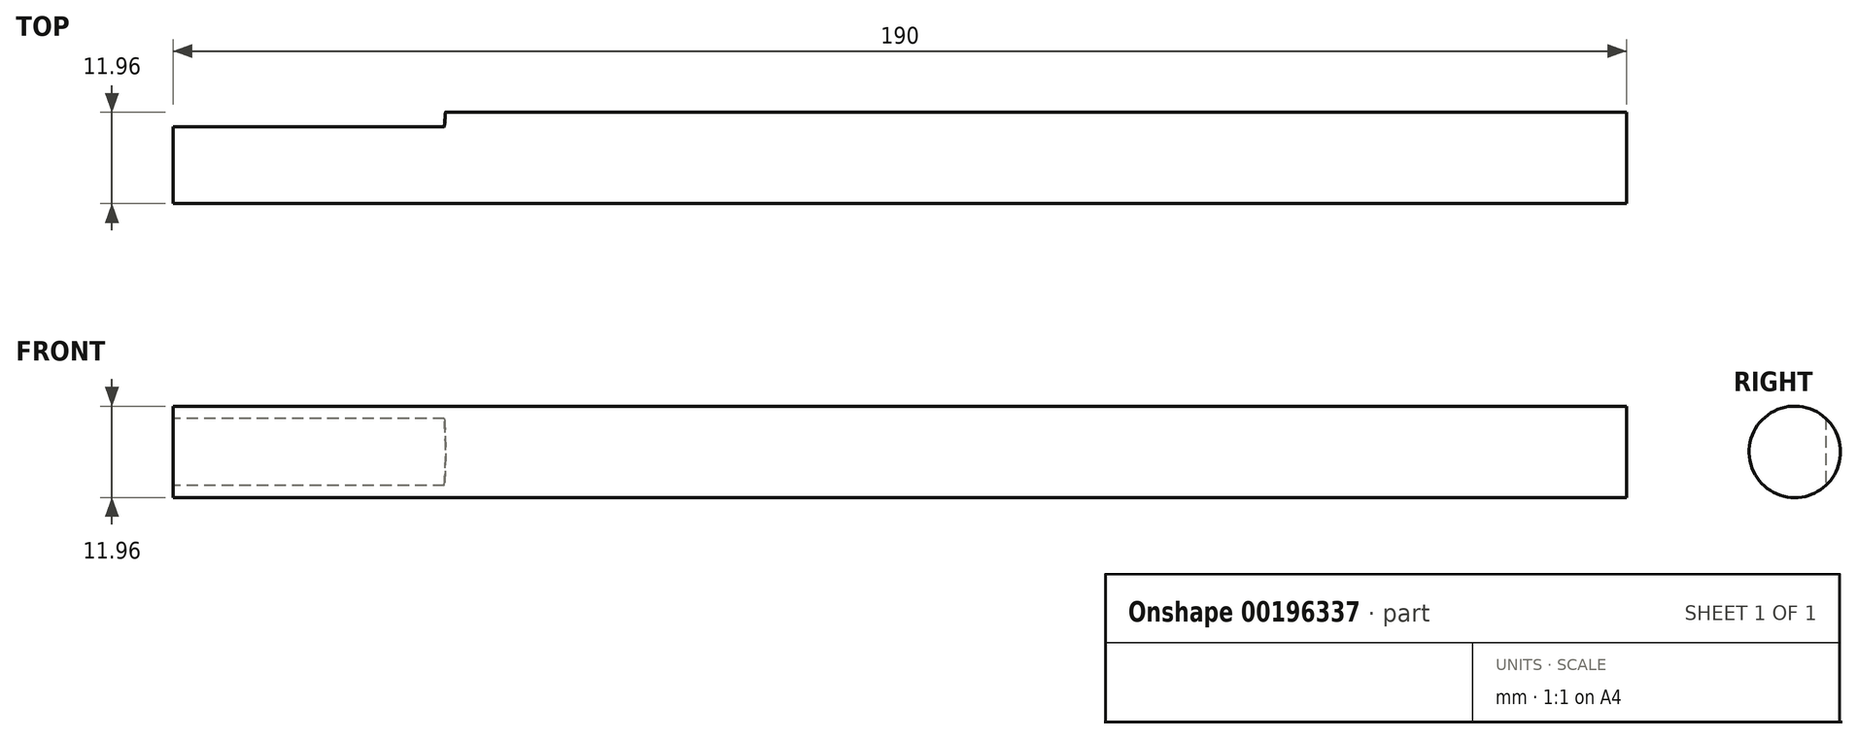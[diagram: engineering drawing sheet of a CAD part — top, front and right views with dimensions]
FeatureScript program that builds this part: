
annotation { "Feature Type Name" : "Feature", "Feature Type Description" : "" }
export const myFeature = defineFeature(function(context is Context, id is Id, definition is map)
    precondition{}
    {
        {
            var Q0;
            Q0=qCreatedBy(makeId("Right.planeOp"),FACE);
            var sketch = newSketch(context, id + "F0", { "sketchPlane" : qUnion([Q0])});
            skCircle(sketch, "E0", {"center": v(0, 0) * mm, "radius": 5.98 * mm});
            skSolve(sketch);
        }
        {
            var Q0;
            Q0 = qSketchRegion(id + "F0", true);
            extrude(context, id + "F1", {"entities" : qUnion([Q0]), "depth" : 200 * mm});
        }
        {
            var Q0;
            Q0=qCreatedBy(makeId("Top.planeOp"),FACE);
            var sketch = newSketch(context, id + "F2", { "sketchPlane" : qUnion([Q0])});
            skLineSegment(sketch, "E1", {"start": v(0, 6.11) * mm, "end": v(45.45, 6.11) * mm});
            skLineSegment(sketch, "E2", {"start": v(45.45, 6.11) * mm, "end": v(45.45, 4.07) * mm});
            skLineSegment(sketch, "E3", {"start": v(45.45, 4.07) * mm, "end": v(0, 4.07) * mm});
            skLineSegment(sketch, "E4", {"start": v(0, 4.07) * mm, "end": v(0, 6.11) * mm});
            skSolve(sketch);
        }
        {
            var Q0;
            Q0 = qSketchRegion(id + "F2", true);
            extrude(context, id + "F3", {"entities" : qUnion([Q0]), "operationType" : NewBodyOperationType.REMOVE, "endBound" : BoundingType.SYMMETRIC, "depth" : 25 * mm});
        }
        {
            var Q0;
            Q0=makeQuery(id+"F3.boolean.opBoolean","COPY",FACE,{"derivedFrom":makeQuery(id+"F3.opExtrude","SWEPT_FACE",FACE,{"disambiguationData":[OSD([sQuery(id+"F2.wireOp",EDGE,"E3")])]})});
            var sketch = newSketch(context, id + "F4", { "sketchPlane" : qUnion([Q0])});
            skLineSegment(sketch, "E5", {"start": v(-45.45, 0) * mm, "end": v(15.43, 0) * mm});
            skCircle(sketch, "E6", {"center": v(15.43, 0) * mm, "radius": 61.04 * mm});
            skSolve(sketch);
        }
        {
            var Q0;
            Q0 = qSketchRegion(id + "F4", true);
            extrude(context, id + "F5", {"entities" : qUnion([Q0]), "operationType" : NewBodyOperationType.REMOVE, "depth" : 25 * mm});
        }
        {
            var Q0;
            Q0=makeQuery(id+"F1.opExtrude","CAP_FACE",FACE,{"disambiguationData":[OSD([sQuery(id+"F0.wireOp",EDGE,"E0")])],"isStart":true});
            var sketch = newSketch(context, id + "F6", { "sketchPlane" : qUnion([Q0])});
            skLineSegment(sketch, "E7.bottom", {"start": v(19.91, 13.65) * mm, "end": v(-32, 13.65) * mm});
            skLineSegment(sketch, "E7.top", {"start": v(19.91, -18.84) * mm, "end": v(-32, -18.84) * mm});
            skLineSegment(sketch, "E7.left", {"start": v(19.91, 13.65) * mm, "end": v(19.91, -18.84) * mm});
            skLineSegment(sketch, "E7.right", {"start": v(-32, 13.65) * mm, "end": v(-32, -18.84) * mm});
            skSolve(sketch);
        }
        {
            var Q0;
            Q0 = qSketchRegion(id + "F6", true);
            extrude(context, id + "F7", {"entities" : qUnion([Q0]), "operationType" : NewBodyOperationType.REMOVE, "oppositeDirection" : true, "depth" : 10 * mm});
        }
    });
